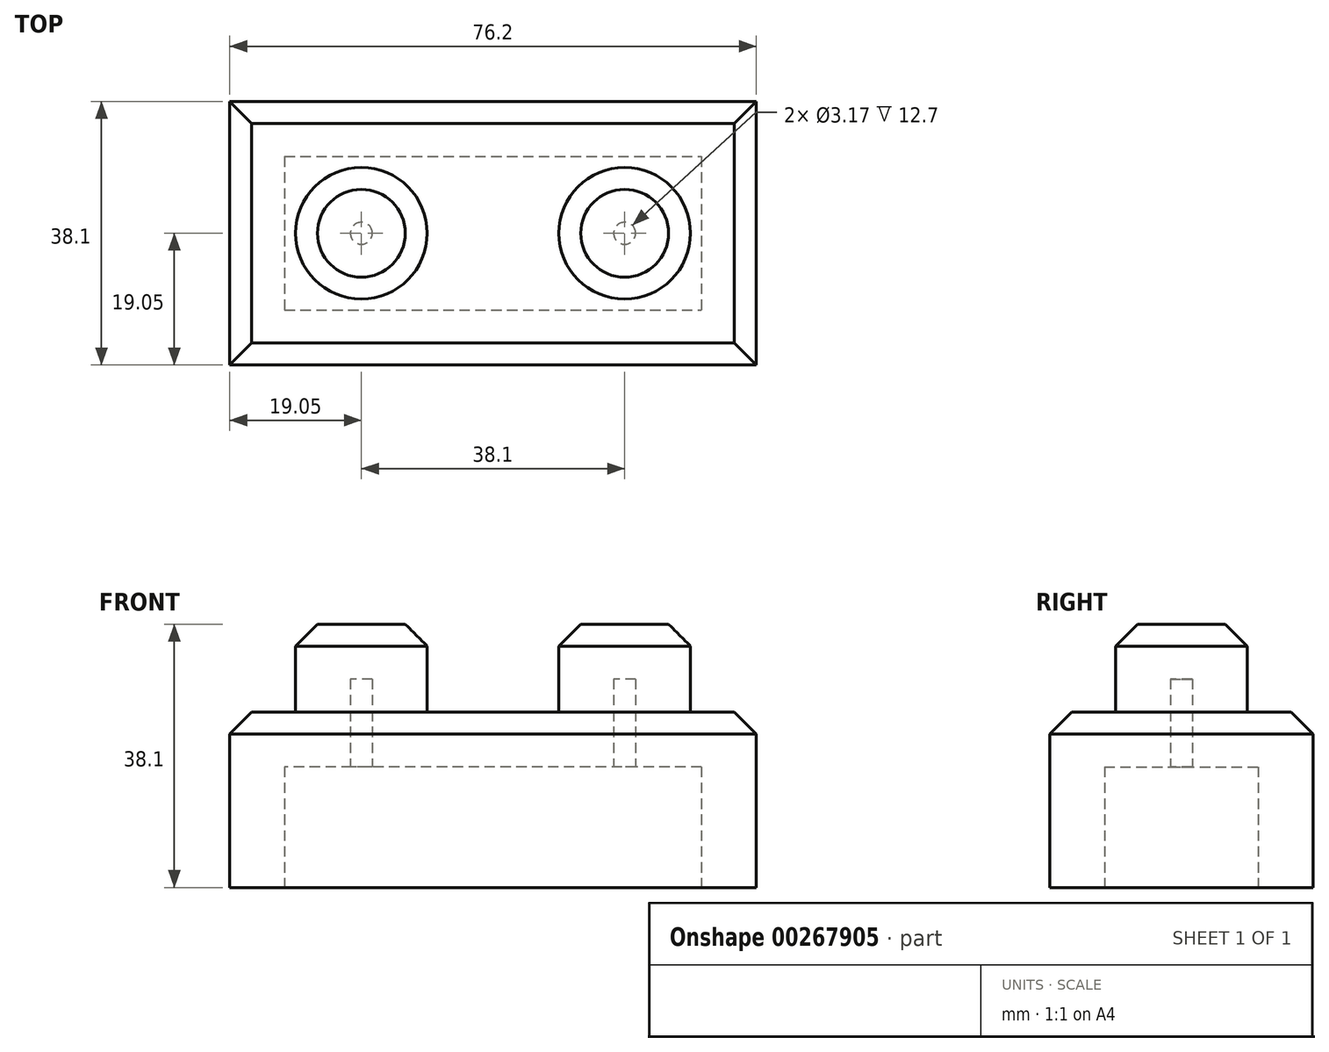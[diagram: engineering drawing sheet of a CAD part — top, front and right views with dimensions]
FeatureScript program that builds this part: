
annotation { "Feature Type Name" : "Feature", "Feature Type Description" : "" }
export const myFeature = defineFeature(function(context is Context, id is Id, definition is map)
    precondition{}
    {
        {
            var Q0;
            Q0=qCreatedBy(makeId("Top.planeOp"),FACE);
            var sketch = newSketch(context, id + "F0", { "sketchPlane" : qUnion([Q0])});
            skLineSegment(sketch, "E0.bottom", {"start": v(0, 0) * mm, "end": v(76.2, 0) * mm});
            skLineSegment(sketch, "E0.top", {"start": v(0, -38.1) * mm, "end": v(76.2, -38.1) * mm});
            skLineSegment(sketch, "E0.left", {"start": v(0, 0) * mm, "end": v(0, -38.1) * mm});
            skLineSegment(sketch, "E0.right", {"start": v(76.2, 0) * mm, "end": v(76.2, -38.1) * mm});
            skSolve(sketch);
        }
        {
            var Q0;
            Q0=qSketchRegion(id+"F0",true);
            extrude(context, id + "F1", {"entities" : qUnion([Q0]), "depth" : 25.4 * mm});
        }
        {
            var Q0;
            Q0=makeQuery(id+"F1.opExtrude","CAP_FACE",FACE,{"disambiguationData":[OSD([sQuery(id+"F0.wireOp",EDGE,"E0.bottom"),sQuery(id+"F0.wireOp",EDGE,"E0.top"),sQuery(id+"F0.wireOp",EDGE,"E0.left"),sQuery(id+"F0.wireOp",EDGE,"E0.right")])],"isStart":false});
            var sketch = newSketch(context, id + "F2", { "sketchPlane" : qUnion([Q0])});
            skCircle(sketch, "E1", {"center": v(19.05, -19.05) * mm, "radius": 9.53 * mm});
            skCircle(sketch, "E2", {"center": v(57.15, -19.05) * mm, "radius": 9.53 * mm});
            skSolve(sketch);
        }
        {
            var Q0;
            Q0=makeQuery(id+"F2.imprint","IMPRINT",FACE,{"disambiguationData":[TD([[makeQuery(id+"F2.imprint","IMPRINT",EDGE,{"derivedFrom":sQuery(id+"F2.wireOp",EDGE,"E1")}),1.0]])]});
            var Q1;
            Q1=makeQuery(id+"F2.imprint","IMPRINT",FACE,{"disambiguationData":[TD([[makeQuery(id+"F2.imprint","IMPRINT",EDGE,{"derivedFrom":sQuery(id+"F2.wireOp",EDGE,"E2")}),1.0]])]});
            extrude(context, id + "F3", {"entities" : qUnion([Q0, Q1]), "operationType" : NewBodyOperationType.ADD, "depth" : 12.7 * mm});
        }
        {
            var Q0;
            Q0=makeQuery(id+"F3.opExtrude","CAP_EDGE",EDGE,{"disambiguationData":[OSD([sQuery(id+"F2.wireOp",EDGE,"E1")])],"isStart":false});
            var Q1;
            Q1=makeQuery(id+"F3.opExtrude","CAP_EDGE",EDGE,{"disambiguationData":[OSD([sQuery(id+"F2.wireOp",EDGE,"E2")])],"isStart":false});
            var Q2;
            Q2=makeQuery(id+"F1.opExtrude","CAP_EDGE",EDGE,{"disambiguationData":[OSD([sQuery(id+"F0.wireOp",EDGE,"E0.top")])],"isStart":false});
            var Q3;
            Q3=makeQuery(id+"F1.opExtrude","CAP_EDGE",EDGE,{"disambiguationData":[OSD([sQuery(id+"F0.wireOp",EDGE,"E0.right")])],"isStart":false});
            var Q4;
            Q4=makeQuery(id+"F1.opExtrude","CAP_EDGE",EDGE,{"disambiguationData":[OSD([sQuery(id+"F0.wireOp",EDGE,"E0.left")])],"isStart":false});
            var Q5;
            Q5=makeQuery(id+"F1.opExtrude","CAP_EDGE",EDGE,{"disambiguationData":[OSD([sQuery(id+"F0.wireOp",EDGE,"E0.bottom")])],"isStart":false});
            chamfer(context, id + "F4", {"entities" : qUnion([Q0, Q1, Q2, Q3, Q4, Q5]), "chamferType" : ChamferType.OFFSET_ANGLE, "width" : 3.17 * mm, "oppositeDirection" : false, "angle" : 45 * degree, "tangentPropagation" : true});
        }
        {
            var Q0;
            Q0=makeQuery(id+"F1.opExtrude","CAP_FACE",FACE,{"disambiguationData":[OSD([sQuery(id+"F0.wireOp",EDGE,"E0.bottom"),sQuery(id+"F0.wireOp",EDGE,"E0.top"),sQuery(id+"F0.wireOp",EDGE,"E0.left"),sQuery(id+"F0.wireOp",EDGE,"E0.right")])],"isStart":true});
            shell(context, id + "F5", {"entities" : qUnion([Q0]), "thickness" : 7.94 * mm});
        }
    });
